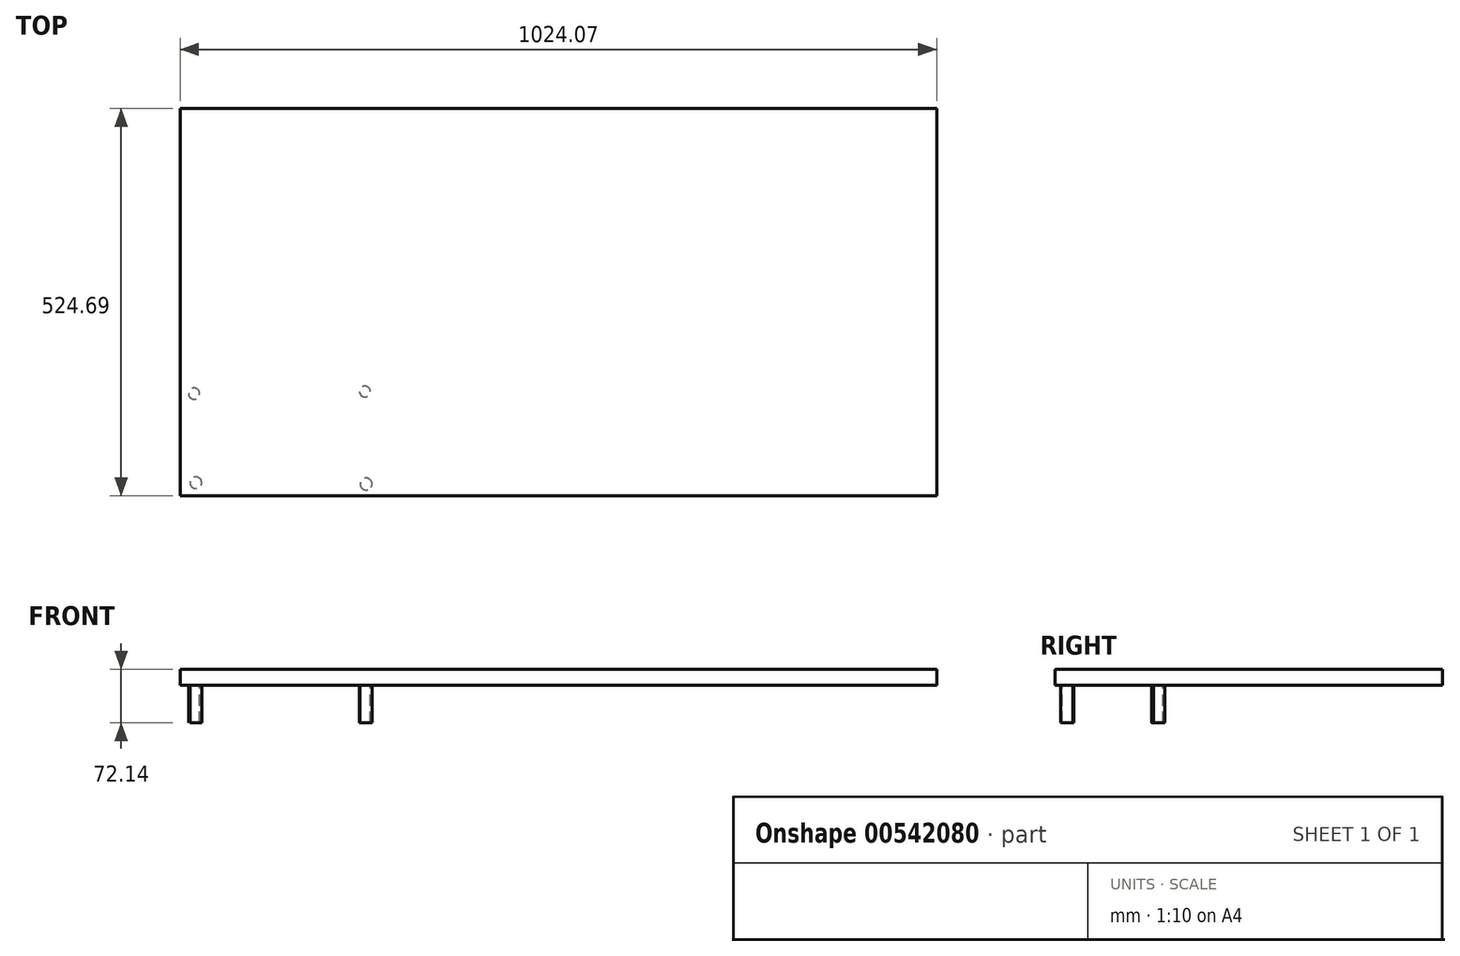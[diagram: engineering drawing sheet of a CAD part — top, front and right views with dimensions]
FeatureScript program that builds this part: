
annotation { "Feature Type Name" : "Feature", "Feature Type Description" : "" }
export const myFeature = defineFeature(function(context is Context, id is Id, definition is map)
    precondition{}
    {
        {
            var Q0;
            Q0=qCreatedBy(makeId("Top.planeOp"),FACE);
            var sketch = newSketch(context, id + "F0", { "sketchPlane" : qUnion([Q0])});
            skLineSegment(sketch, "E0.bottom", {"start": v(-138.95, -32.8) * mm, "end": v(885.12, -32.8) * mm});
            skLineSegment(sketch, "E0.top", {"start": v(-138.95, 491.9) * mm, "end": v(885.12, 491.9) * mm});
            skLineSegment(sketch, "E0.left", {"start": v(-138.95, -32.8) * mm, "end": v(-138.95, 491.9) * mm});
            skLineSegment(sketch, "E0.right", {"start": v(885.12, -32.8) * mm, "end": v(885.12, 491.9) * mm});
            skSolve(sketch);
        }
        {
            var Q0;
            Q0=makeQuery(id+"F0.imprint","IMPRINT",FACE,{"disambiguationData":[TD([[makeQuery(id+"F0.imprint","IMPRINT",EDGE,{"derivedFrom":sQuery(id+"F0.wireOp",EDGE,"E0.bottom")}),1.0]])]});
            extrude(context, id + "F1", {"entities" : qUnion([Q0]), "oppositeDirection" : true, "depth" : 21.34 * mm, "offsetDistance" : 25.4 * mm});
        }
        {
            var Q0;
            Q0=makeQuery(id+"F1.opExtrude","CAP_FACE",FACE,{"disambiguationData":[OSD([sQuery(id+"F0.wireOp",EDGE,"E0.bottom"),sQuery(id+"F0.wireOp",EDGE,"E0.top"),sQuery(id+"F0.wireOp",EDGE,"E0.left"),sQuery(id+"F0.wireOp",EDGE,"E0.right")])],"isStart":false});
            var sketch = newSketch(context, id + "F2", { "sketchPlane" : qUnion([Q0])});
            skCircle(sketch, "E1", {"center": v(-117.82, 14.96) * mm, "radius": 7.88 * mm});
            skSolve(sketch);
        }
        {
            var Q0;
            Q0=makeQuery(id+"F2.imprint","IMPRINT",FACE,{"disambiguationData":[TD([[makeQuery(id+"F2.imprint","IMPRINT",EDGE,{"derivedFrom":sQuery(id+"F2.wireOp",EDGE,"E1")}),1.0]])]});
            extrude(context, id + "F3", {"entities" : qUnion([Q0]), "operationType" : NewBodyOperationType.ADD, "depth" : 50.8 * mm, "offsetDistance" : 25.4 * mm});
        }
        {
            var Q0;
            Q0=makeQuery(id+"F1.opExtrude","CAP_FACE",FACE,{"disambiguationData":[OSD([sQuery(id+"F0.wireOp",EDGE,"E0.bottom"),sQuery(id+"F0.wireOp",EDGE,"E0.top"),sQuery(id+"F0.wireOp",EDGE,"E0.left"),sQuery(id+"F0.wireOp",EDGE,"E0.right")])],"isStart":false});
            var sketch = newSketch(context, id + "F4", { "sketchPlane" : qUnion([Q0])});
            skCircle(sketch, "E2", {"center": v(-120.25, -105.7) * mm, "radius": 7.57 * mm});
            skSolve(sketch);
        }
        {
            var Q0;
            Q0=makeQuery(id+"F4.imprint","IMPRINT",FACE,{"disambiguationData":[TD([[makeQuery(id+"F4.imprint","IMPRINT",EDGE,{"derivedFrom":sQuery(id+"F4.wireOp",EDGE,"E2")}),1.0]])]});
            extrude(context, id + "F5", {"entities" : qUnion([Q0]), "operationType" : NewBodyOperationType.ADD, "depth" : 50.8 * mm, "offsetDistance" : 25.4 * mm});
        }
        {
            var Q0;
            Q0=makeQuery(id+"F1.opExtrude","CAP_FACE",FACE,{"disambiguationData":[OSD([sQuery(id+"F0.wireOp",EDGE,"E0.bottom"),sQuery(id+"F0.wireOp",EDGE,"E0.top"),sQuery(id+"F0.wireOp",EDGE,"E0.left"),sQuery(id+"F0.wireOp",EDGE,"E0.right")])],"isStart":false});
            var sketch = newSketch(context, id + "F6", { "sketchPlane" : qUnion([Q0])});
            skCircle(sketch, "E3", {"center": v(111.06, -108.45) * mm, "radius": 7.37 * mm});
            skSolve(sketch);
        }
        {
            var Q0;
            Q0=makeQuery(id+"F6.imprint","IMPRINT",FACE,{"disambiguationData":[TD([[makeQuery(id+"F6.imprint","IMPRINT",EDGE,{"derivedFrom":sQuery(id+"F6.wireOp",EDGE,"E3")}),1.0]])]});
            extrude(context, id + "F7", {"entities" : qUnion([Q0]), "operationType" : NewBodyOperationType.ADD, "depth" : 50.8 * mm, "offsetDistance" : 25.4 * mm});
        }
        {
            var Q0;
            Q0=makeQuery(id+"F1.opExtrude","CAP_FACE",FACE,{"disambiguationData":[OSD([sQuery(id+"F0.wireOp",EDGE,"E0.bottom"),sQuery(id+"F0.wireOp",EDGE,"E0.top"),sQuery(id+"F0.wireOp",EDGE,"E0.left"),sQuery(id+"F0.wireOp",EDGE,"E0.right")])],"isStart":false});
            var sketch = newSketch(context, id + "F8", { "sketchPlane" : qUnion([Q0])});
            skCircle(sketch, "E4", {"center": v(112.67, 16.72) * mm, "radius": 8.11 * mm});
            skSolve(sketch);
        }
        {
            var Q0;
            Q0=makeQuery(id+"F8.imprint","IMPRINT",FACE,{"disambiguationData":[TD([[makeQuery(id+"F8.imprint","IMPRINT",EDGE,{"derivedFrom":sQuery(id+"F8.wireOp",EDGE,"E4")}),1.0]])]});
            extrude(context, id + "F9", {"entities" : qUnion([Q0]), "operationType" : NewBodyOperationType.ADD, "depth" : 50.8 * mm, "offsetDistance" : 25.4 * mm});
        }
    });
